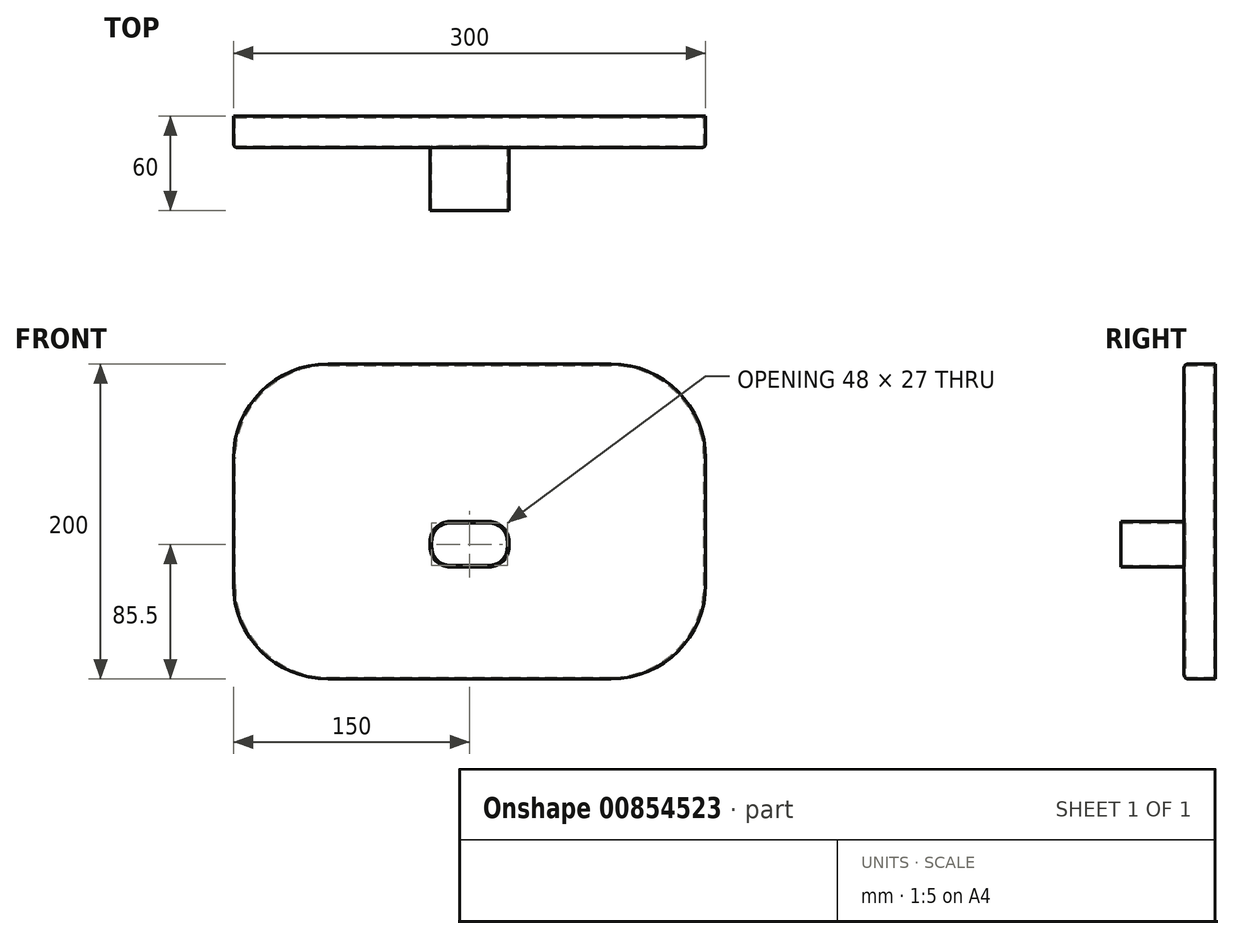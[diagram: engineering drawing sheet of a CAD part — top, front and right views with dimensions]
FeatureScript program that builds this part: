
annotation { "Feature Type Name" : "Feature", "Feature Type Description" : "" }
export const myFeature = defineFeature(function(context is Context, id is Id, definition is map)
    precondition{}
    {
        {
            var Q0;
            Q0=qCreatedBy(makeId("Front.planeOp"),FACE);
            var sketch = newSketch(context, id + "F0", { "sketchPlane" : qUnion([Q0])});
            skLineSegment(sketch, "E0.bottom", {"start": v(60, 0) * mm, "end": v(240, 0) * mm});
            skLineSegment(sketch, "E0.top", {"start": v(60, 200) * mm, "end": v(240, 200) * mm});
            skLineSegment(sketch, "E0.left", {"start": v(0, 60) * mm, "end": v(0, 140) * mm});
            skLineSegment(sketch, "E0.right", {"start": v(300, 60) * mm, "end": v(300, 140) * mm});
            skPoint(sketch, "E1.visualSharp", {"position": v(300, 0) * mm});
            skArc(sketch, "E1.filletArc", {"start": v(240, 0) * mm, "mid": v(282.43, 17.57) * mm, "end": v(300, 60) * mm});
            skPoint(sketch, "E2.visualSharp", {"position": v(0, 0) * mm});
            skArc(sketch, "E2.filletArc", {"start": v(0, 60) * mm, "mid": v(17.57, 17.57) * mm, "end": v(60, 0) * mm});
            skPoint(sketch, "E3.visualSharp", {"position": v(0, 200) * mm});
            skArc(sketch, "E3.filletArc", {"start": v(60, 200) * mm, "mid": v(17.57, 182.43) * mm, "end": v(0, 140) * mm});
            skPoint(sketch, "E4.visualSharp", {"position": v(300, 200) * mm});
            skArc(sketch, "E4.filletArc", {"start": v(300, 140) * mm, "mid": v(282.43, 182.43) * mm, "end": v(240, 200) * mm});
            skSolve(sketch);
        }
        {
            var Q0;
            Q0=makeQuery(id+"F0.imprint","IMPRINT",FACE,{"disambiguationData":[TD([[makeQuery(id+"F0.imprint","IMPRINT",EDGE,{"derivedFrom":sQuery(id+"F0.wireOp",EDGE,"E0.bottom")}),1.0]])]});
            extrude(context, id + "F1", {"entities" : qUnion([Q0]), "depth" : 20 * mm, "offsetDistance" : 25.4 * mm});
        }
        {
            var Q0;
            Q0=makeQuery(id+"F1.opExtrude","CAP_FACE",FACE,{"disambiguationData":[OSD([sQuery(id+"F0.wireOp",EDGE,"E0.bottom"),sQuery(id+"F0.wireOp",EDGE,"E0.top"),sQuery(id+"F0.wireOp",EDGE,"E0.left"),sQuery(id+"F0.wireOp",EDGE,"E0.right")])],"isStart":false});
            var sketch = newSketch(context, id + "F2", { "sketchPlane" : qUnion([Q0])});
            skLineSegment(sketch, "E5", {"start": v(175, 85.5) * mm, "end": v(175, 87.3) * mm});
            skLineSegment(sketch, "E6", {"start": v(162.3, 100) * mm, "end": v(137.7, 100) * mm});
            skLineSegment(sketch, "E7", {"start": v(125, 87.3) * mm, "end": v(125, 85.5) * mm});
            skLineSegment(sketch, "E8", {"start": v(125, 85.5) * mm, "end": v(125, 83.7) * mm});
            skLineSegment(sketch, "E9", {"start": v(137.7, 71) * mm, "end": v(162.3, 71) * mm});
            skLineSegment(sketch, "E10", {"start": v(175, 83.7) * mm, "end": v(175, 85.5) * mm});
            skPoint(sketch, "E11.visualSharp", {"position": v(125, 100) * mm});
            skArc(sketch, "E11.filletArc", {"start": v(137.7, 100) * mm, "mid": v(128.72, 96.28) * mm, "end": v(125, 87.3) * mm});
            skPoint(sketch, "E12.visualSharp", {"position": v(125, 71) * mm});
            skArc(sketch, "E12.filletArc", {"start": v(125, 83.7) * mm, "mid": v(128.72, 74.72) * mm, "end": v(137.7, 71) * mm});
            skPoint(sketch, "E13.visualSharp", {"position": v(175, 100) * mm});
            skArc(sketch, "E13.filletArc", {"start": v(175, 87.3) * mm, "mid": v(171.28, 96.28) * mm, "end": v(162.3, 100) * mm});
            skPoint(sketch, "E14.visualSharp", {"position": v(175, 71) * mm});
            skArc(sketch, "E14.filletArc", {"start": v(162.3, 71) * mm, "mid": v(171.28, 74.72) * mm, "end": v(175, 83.7) * mm});
            skLineSegment(sketch, "E15", {"start": v(162.3, 100) * mm, "end": v(150, 100) * mm});
            skPoint(sketch, "E16", {"position": v(150, 100) * mm});
            skPoint(sketch, "E17", {"position": v(150, 85.5) * mm});
            skSolve(sketch);
        }
        {
            var Q0;
            Q0=makeQuery(id+"F2.imprint","IMPRINT",FACE,{"disambiguationData":[TD([[makeQuery(id+"F2.imprint","IMPRINT",EDGE,{"derivedFrom":sQuery(id+"F2.wireOp",EDGE,"E5")}),1.0]])]});
            extrude(context, id + "F3", {"entities" : qUnion([Q0]), "operationType" : NewBodyOperationType.ADD, "depth" : 40 * mm, "offsetDistance" : 25.4 * mm});
        }
        {
            var Q0;
            Q0=makeQuery(id+"F3.opExtrude","CAP_FACE",FACE,{"disambiguationData":[OSD([sQuery(id+"F2.wireOp",EDGE,"E5"),sQuery(id+"F2.wireOp",EDGE,"E6"),sQuery(id+"F2.wireOp",EDGE,"E7"),sQuery(id+"F2.wireOp",EDGE,"E8"),sQuery(id+"F2.wireOp",EDGE,"E9"),sQuery(id+"F2.wireOp",EDGE,"E10"),sQuery(id+"F2.wireOp",EDGE,"E11.filletArc"),sQuery(id+"F2.wireOp",EDGE,"E12.filletArc"),sQuery(id+"F2.wireOp",EDGE,"E13.filletArc"),sQuery(id+"F2.wireOp",EDGE,"E14.filletArc")])],"isStart":false});
            shell(context, id + "F4", {"entities" : qUnion([Q0]), "thickness" : 1 * mm});
        }
        {
            var Q0;
            Q0=makeQuery(id+"F1.opExtrude","CAP_EDGE",EDGE,{"disambiguationData":[OSD([sQuery(id+"F0.wireOp",EDGE,"E0.right")])],"isStart":false});
            var Q1;
            Q1=makeQuery(id+"F1.opExtrude","CAP_EDGE",EDGE,{"disambiguationData":[OSD([sQuery(id+"F0.wireOp",EDGE,"E0.top")])],"isStart":false});
            var Q2;
            Q2=makeQuery(id+"F1.opExtrude","CAP_EDGE",EDGE,{"disambiguationData":[OSD([sQuery(id+"F0.wireOp",EDGE,"E0.left")])],"isStart":false});
            var Q3;
            Q3=makeQuery(id+"F1.opExtrude","CAP_EDGE",EDGE,{"disambiguationData":[OSD([sQuery(id+"F0.wireOp",EDGE,"E0.bottom")])],"isStart":false});
            fillet(context, id + "F5", {"entities" : qUnion([Q0, Q1, Q2, Q3]), "radius" : 2.54 * mm, "tangentPropagation" : true, "allowEdgeOverflow" : false});
        }
    });
